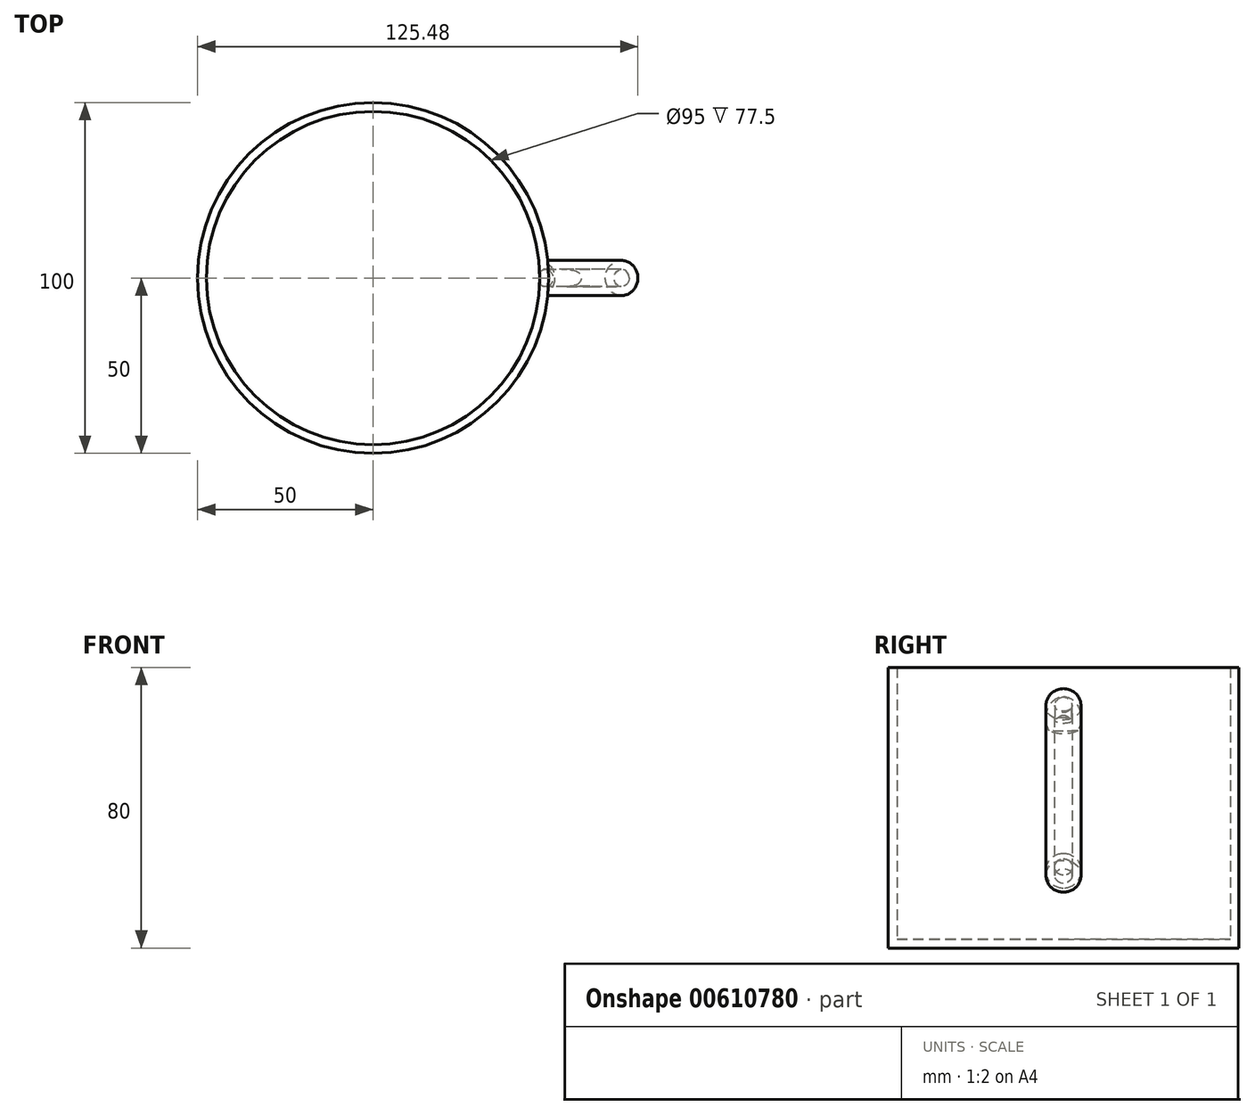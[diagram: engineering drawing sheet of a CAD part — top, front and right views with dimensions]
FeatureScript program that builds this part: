
annotation { "Feature Type Name" : "Feature", "Feature Type Description" : "" }
export const myFeature = defineFeature(function(context is Context, id is Id, definition is map)
    precondition{}
    {
        {
            var Q0;
            Q0=qCreatedBy(makeId("Top.planeOp"),FACE);
            var sketch = newSketch(context, id + "F0", { "sketchPlane" : qUnion([Q0])});
            skCircle(sketch, "E0", {"center": v(0, 0) * mm, "radius": 50 * mm});
            skSolve(sketch);
        }
        {
            var Q0;
            Q0 = qSketchRegion(id + "F0", true);
            extrude(context, id + "F1", {"entities" : qUnion([Q0]), "depth" : 80 * mm, "offsetDistance" : 25.4 * mm});
        }
        {
            var Q0;
            Q0=qCreatedBy(makeId("Right.planeOp"),FACE);
            cPlane(context, id + "F2", {"entities" : qUnion([Q0]), "cplaneType" : CPlaneType.OFFSET, "offset" : 50 * mm, "width" : 152.4 * mm, "height" : 152.4 * mm});
        }
        {
            var Q0;
            Q0=qCreatedBy(makeId("Front.planeOp"),FACE);
            var sketch = newSketch(context, id + "F3", { "sketchPlane" : qUnion([Q0])});
            skFitSpline(sketch, "E1", {"points": [v(47.34, 63) * mm, v(57.32, 68.93) * mm, v(68.38, 55.99) * mm, v(68.11, 30.09) * mm, v(57.05, 20.92) * mm, v(46.8, 23.62) * mm], "startDerivative": vector(56.6, 54.6) * mm, "endDerivative": vector(-60.7, 28.82) * mm});
            skSolve(sketch);
        }
        {
            var Q0;
            Q0=qCreatedBy(id+"F2.planeOp",FACE);
            var sketch = newSketch(context, id + "F4", { "sketchPlane" : qUnion([Q0])});
            skCircle(sketch, "E2", {"center": v(0, 22) * mm, "radius": 5 * mm});
            skSolve(sketch);
        }
        {
            var Q0;
            Q0=makeQuery(id+"F4.imprint","IMPRINT",FACE,{"disambiguationData":[TD([[makeQuery(id+"F4.imprint","IMPRINT",EDGE,{"derivedFrom":sQuery(id+"F4.wireOp",EDGE,"E2")}),1.0]])]});
            var Q1;
            Q1=sQuery(id+"F3.wireOp",EDGE,"E1");
            sweep(context, id + "F5", {"operationType" : NewBodyOperationType.ADD, "profiles" : qUnion([Q0]), "path" : qUnion([Q1])});
        }
        {
            var Q0;
            Q0=makeQuery(id+"F1.opExtrude","CAP_FACE",FACE,{"disambiguationData":[OSD([sQuery(id+"F0.wireOp",EDGE,"E0")])],"isStart":false});
            shell(context, id + "F6", {"entities" : qUnion([Q0]), "thickness" : 2.5 * mm});
        }
    });
